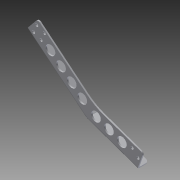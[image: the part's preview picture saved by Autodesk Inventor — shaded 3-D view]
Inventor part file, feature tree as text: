
AUTODESK INVENTOR PART (.ipt)
format: ipt  version: 2014 SP1 (Build 180222100, 222)  size: 183,808 bytes
history: native  units: in
note: dims shown in document units (in); Inventor stores cm internally (conversion verified against a paired STEP export)
features: other x3, sketch x1
ambient origin geometry x8: Origin, YZ Plane, XZ Plane, XY Plane, X Axis, Y Axis, Z Axis, Center Point
bodies: Solid1 (feature_tree)
feature tree (4):
  other  "V5 Shooter Frame Channel P5.ipt"
  other  "Solid1::V5 Shooter Frame Channel P5.ipt"
  sketch  "Sketch1"  dims[d0=0.3937in]
  other  "TaggingFeature1"
